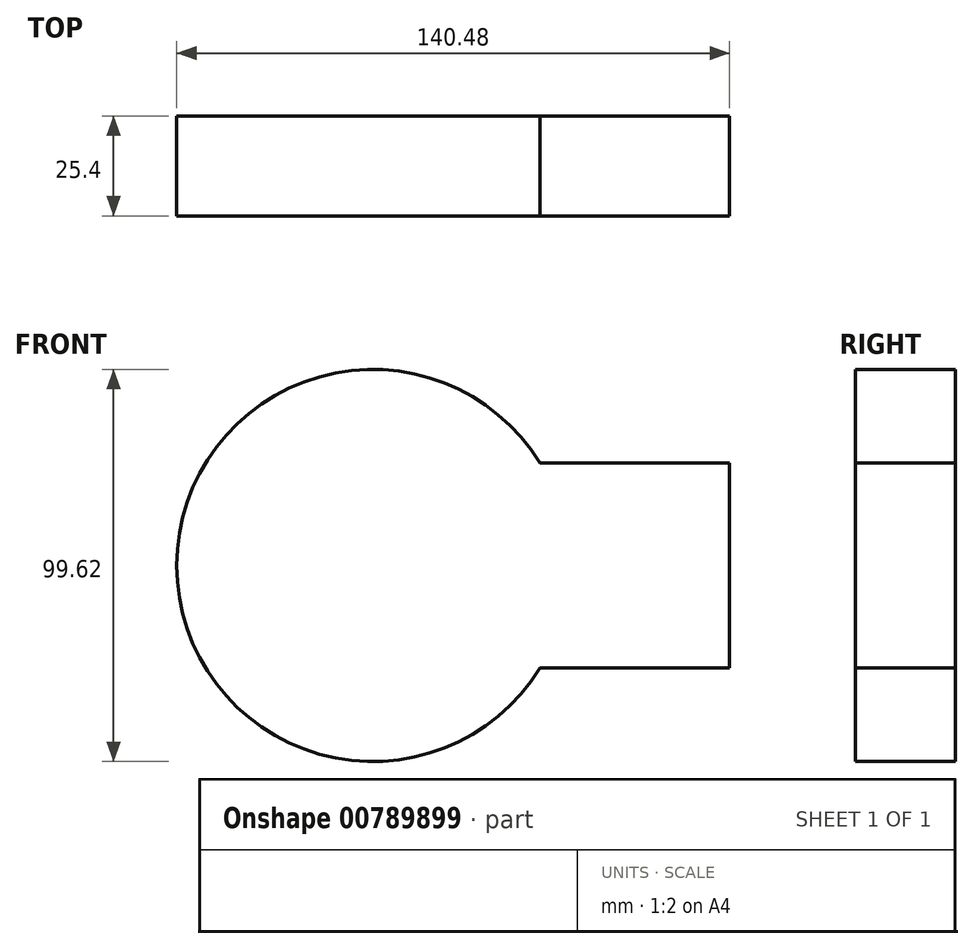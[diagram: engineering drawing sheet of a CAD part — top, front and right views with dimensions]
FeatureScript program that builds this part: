
annotation { "Feature Type Name" : "Feature", "Feature Type Description" : "" }
export const myFeature = defineFeature(function(context is Context, id is Id, definition is map)
    precondition{}
    {
        {
            var Q0;
            Q0=qCreatedBy(makeId("Front.planeOp"),FACE);
            var sketch = newSketch(context, id + "F0", { "sketchPlane" : qUnion([Q0])});
            skArc(sketch, "E0", {"start": v(42.5, 25.99) * mm, "mid": v(-49.8, 0) * mm, "end": v(42.5, -25.99) * mm});
            skLineSegment(sketch, "E1.bottom", {"start": v(42.5, 25.99) * mm, "end": v(90.67, 25.99) * mm});
            skLineSegment(sketch, "E1.top", {"start": v(42.5, -25.99) * mm, "end": v(90.67, -25.99) * mm});
            skLineSegment(sketch, "E1.right", {"start": v(90.67, 25.99) * mm, "end": v(90.67, -25.99) * mm});
            skSolve(sketch);
        }
        {
            var Q0;
            Q0=makeQuery(id+"F0.imprint","IMPRINT",FACE,{"disambiguationData":[TD([[makeQuery(id+"F0.imprint","IMPRINT",EDGE,{"derivedFrom":sQuery(id+"F0.wireOp",EDGE,"E0")}),1.0]])]});
            extrude(context, id + "F1", {"entities" : qUnion([Q0]), "depth" : 25.4 * mm, "offsetDistance" : 25.4 * mm});
        }
    });
